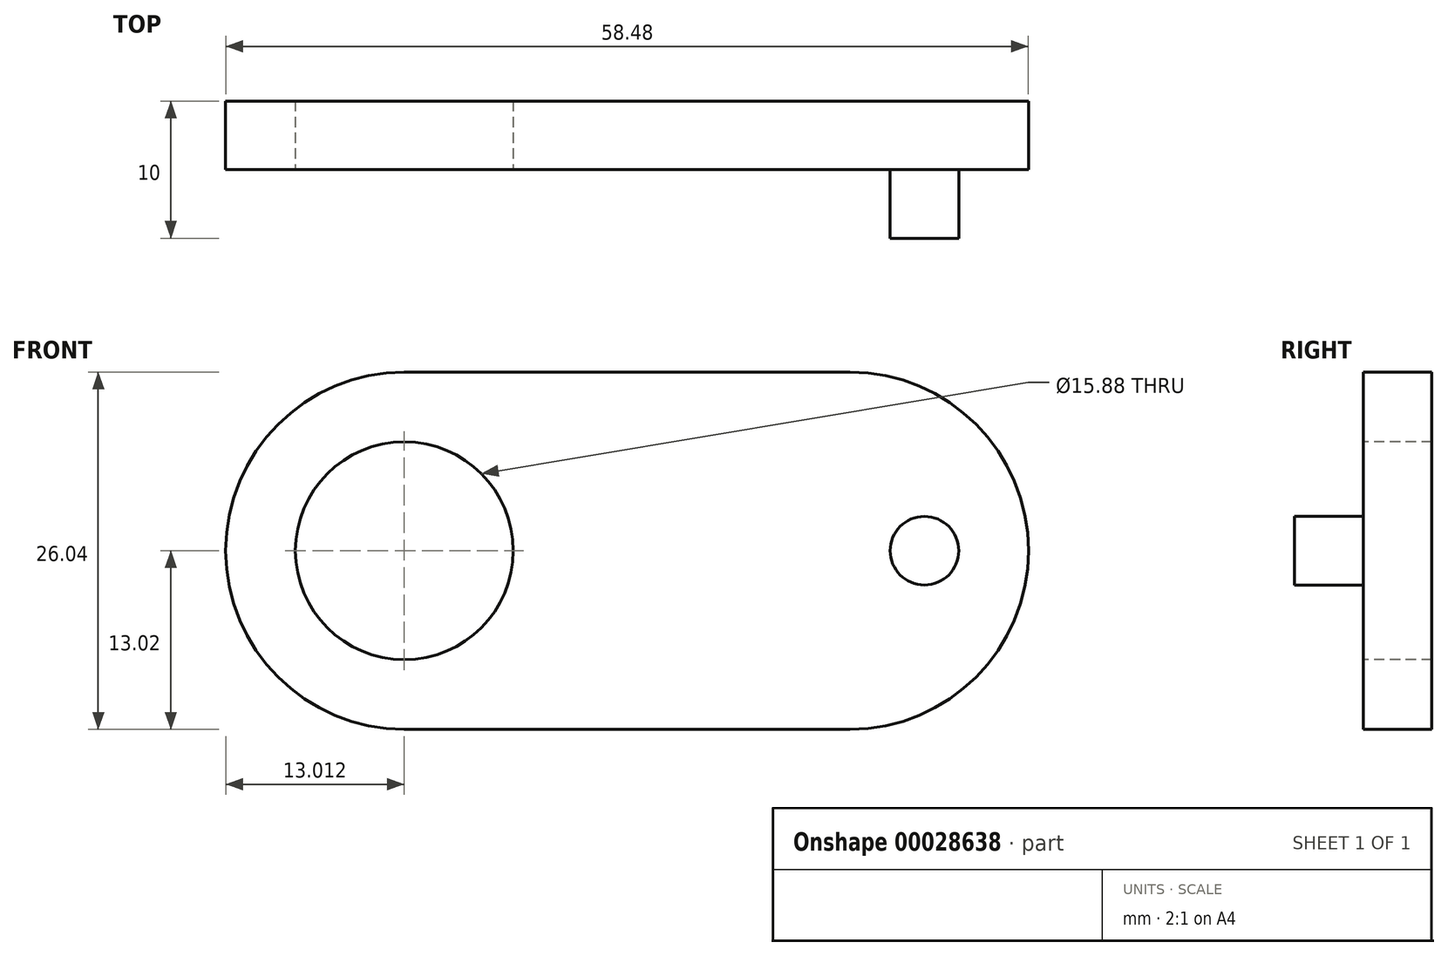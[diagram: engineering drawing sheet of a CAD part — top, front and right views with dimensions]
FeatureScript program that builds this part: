
annotation { "Feature Type Name" : "Feature", "Feature Type Description" : "" }
export const myFeature = defineFeature(function(context is Context, id is Id, definition is map)
    precondition{}
    {
        {
            var Q0;
            Q0=qCreatedBy(makeId("Front.planeOp"),FACE);
            var sketch = newSketch(context, id + "F0", { "sketchPlane" : qUnion([Q0])});
            skLineSegment(sketch, "E0.rect.bottom", {"start": v(29.24, -13.02) * mm, "end": v(-29.24, -13.02) * mm});
            skLineSegment(sketch, "E0.rect.top", {"start": v(29.24, 13.02) * mm, "end": v(-29.24, 13.02) * mm});
            skLineSegment(sketch, "E0.rect.left", {"start": v(29.24, -13.02) * mm, "end": v(29.24, 13.02) * mm});
            skLineSegment(sketch, "E0.rect.right", {"start": v(-29.24, -13.02) * mm, "end": v(-29.24, 13.02) * mm});
            skPoint(sketch, "E0.rect.middle", {"position": v(0, 0) * mm});
            skCircle(sketch, "E1", {"center": v(16.23, 0) * mm, "radius": 13.02 * mm});
            skCircle(sketch, "E2", {"center": v(-16.23, 0) * mm, "radius": 13.02 * mm});
            skSolve(sketch);
        }
        {
            var Q0;
            {var subQ0=sQuery(id+"F0.wireOp",EDGE,"E2");var subQ1=makeQuery(id+"F0.imprint","INTERSECT",VERTEX,{"derivedFrom":[sQuery(id+"F0.wireOp",EDGE,"E0.rect.top"),subQ0]});Q0=makeQuery(id+"F0.imprint","IMPRINT",FACE,{"disambiguationData":[TD([[makeQuery(id+"F0.imprint","IMPRINT",EDGE,{"disambiguationData":[TD([[subQ1,-1.0]])],"derivedFrom":subQ0}),1.0]])]});}
            var Q1;
            {var subQ3=sQuery(id+"F0.wireOp",EDGE,"E0.rect.bottom");var subQ5=sQuery(id+"F0.wireOp",EDGE,"E1");var subQ7=makeQuery(id+"F0.imprint","INTERSECT",VERTEX,{"derivedFrom":[subQ3,subQ5]});Q1=makeQuery(id+"F0.imprint","IMPRINT",FACE,{"disambiguationData":[TD([[makeQuery(id+"F0.imprint","IMPRINT",EDGE,{"disambiguationData":[TD([[subQ7,-1.0]])],"derivedFrom":subQ3}),-1.0]])]});}
            var Q2;
            {var subQ0=sQuery(id+"F0.wireOp",EDGE,"E1");var subQ3=makeQuery(id+"F0.imprint","INTERSECT",VERTEX,{"derivedFrom":[sQuery(id+"F0.wireOp",EDGE,"E0.rect.top"),subQ0]});Q2=makeQuery(id+"F0.imprint","IMPRINT",FACE,{"disambiguationData":[TD([[makeQuery(id+"F0.imprint","IMPRINT",EDGE,{"disambiguationData":[TD([[subQ3,1.0]])],"derivedFrom":subQ0}),1.0]])]});}
            extrude(context, id + "F1", {"entities" : qUnion([Q0, Q1, Q2]), "endBound" : BoundingType.SYMMETRIC, "depth" : 5 * mm});
        }
        {
            var Q0;
            Q0=makeQuery(id+"F1.opExtrude","CAP_FACE",FACE,{"disambiguationData":[OSD([sQuery(id+"F0.wireOp",EDGE,"E0.rect.bottom"),sQuery(id+"F0.wireOp",EDGE,"E0.rect.top"),sQuery(id+"F0.wireOp",EDGE,"E1"),sQuery(id+"F0.wireOp",EDGE,"E2")])],"isStart":false});
            var sketch = newSketch(context, id + "F2", { "sketchPlane" : qUnion([Q0])});
            skCircle(sketch, "E3", {"center": v(21.66, 0) * mm, "radius": 2.5 * mm});
            skSolve(sketch);
        }
        {
            var Q0;
            Q0=makeQuery(id+"F2.imprint","IMPRINT",FACE,{"disambiguationData":[TD([[makeQuery(id+"F2.imprint","IMPRINT",EDGE,{"derivedFrom":sQuery(id+"F2.wireOp",EDGE,"E3")}),1.0]])]});
            extrude(context, id + "F3", {"entities" : qUnion([Q0]), "operationType" : NewBodyOperationType.ADD, "depth" : 5 * mm});
        }
        {
            var Q0;
            Q0=makeQuery(id+"F1.opExtrude","CAP_FACE",FACE,{"disambiguationData":[OSD([sQuery(id+"F0.wireOp",EDGE,"E0.rect.bottom"),sQuery(id+"F0.wireOp",EDGE,"E0.rect.top"),sQuery(id+"F0.wireOp",EDGE,"E1"),sQuery(id+"F0.wireOp",EDGE,"E2")])],"isStart":false});
            var sketch = newSketch(context, id + "F4", { "sketchPlane" : qUnion([Q0])});
            skCircle(sketch, "E4", {"center": v(-16.23, 0) * mm, "radius": 7.94 * mm});
            skSolve(sketch);
        }
        {
            var Q0;
            Q0=makeQuery(id+"F4.imprint","IMPRINT",FACE,{"disambiguationData":[TD([[makeQuery(id+"F4.imprint","IMPRINT",EDGE,{"derivedFrom":sQuery(id+"F4.wireOp",EDGE,"E4")}),1.0]])]});
            var Q1;
            Q1=makeQuery(id+"F1.opExtrude","CAP_FACE",FACE,{"disambiguationData":[OSD([sQuery(id+"F0.wireOp",EDGE,"E0.rect.bottom"),sQuery(id+"F0.wireOp",EDGE,"E0.rect.top"),sQuery(id+"F0.wireOp",EDGE,"E1"),sQuery(id+"F0.wireOp",EDGE,"E2")])],"isStart":true});
            extrude(context, id + "F5", {"entities" : qUnion([Q0]), "operationType" : NewBodyOperationType.REMOVE, "endBound" : BoundingType.UP_TO_SURFACE, "oppositeDirection" : true, "endBoundEntityFace" : qUnion([Q1]), "depth" : 25.4 * mm});
        }
    });
